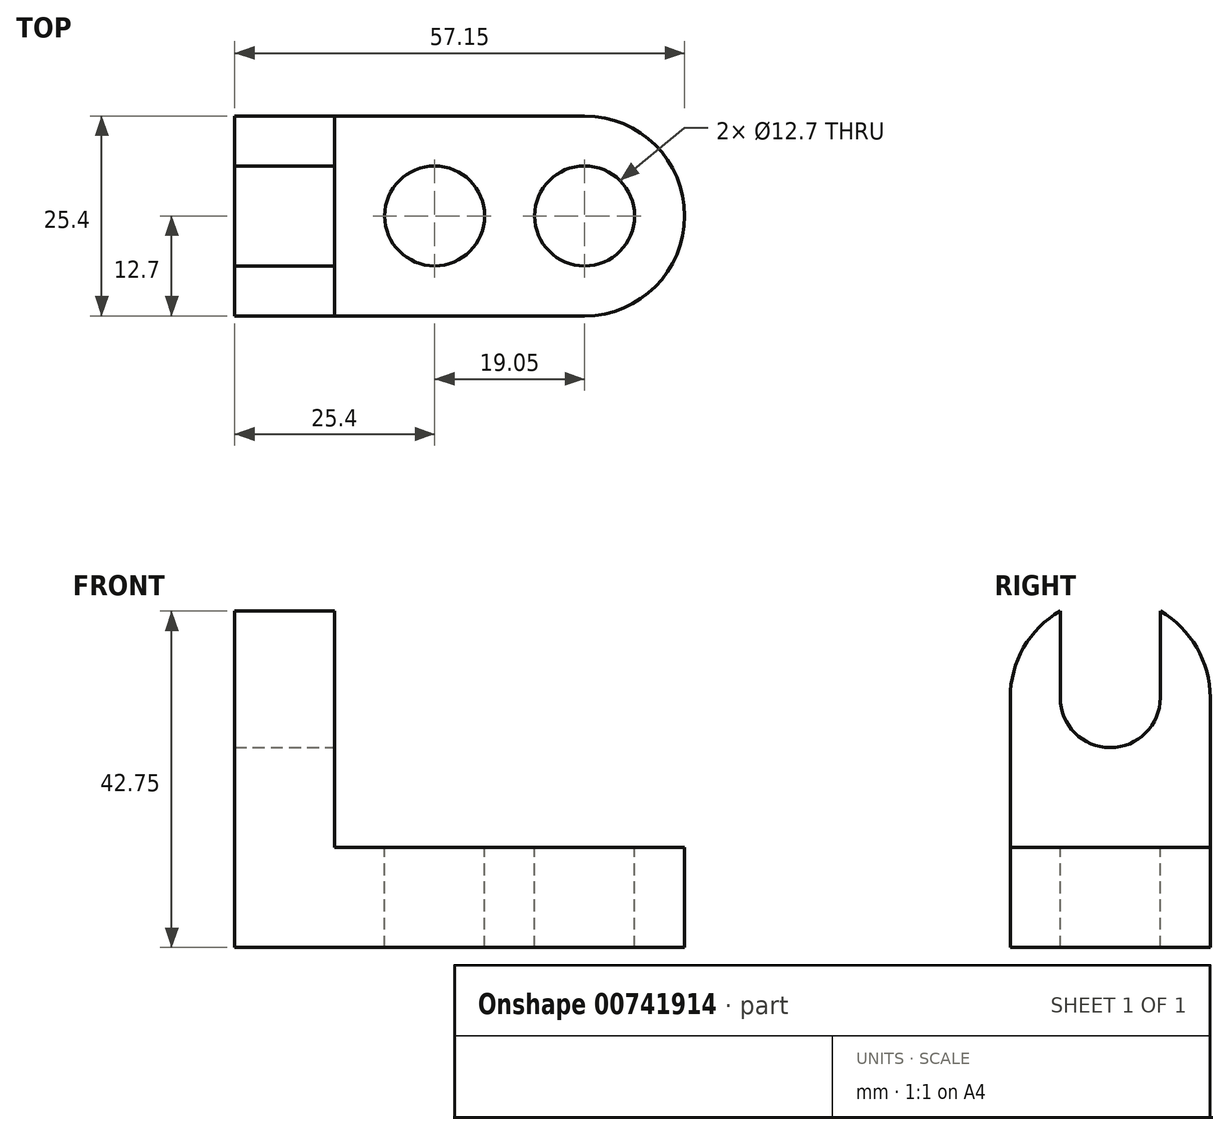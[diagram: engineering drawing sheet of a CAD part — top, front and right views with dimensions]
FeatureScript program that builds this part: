
annotation { "Feature Type Name" : "Feature", "Feature Type Description" : "" }
export const myFeature = defineFeature(function(context is Context, id is Id, definition is map)
    precondition{}
    {
        {
            var Q0;
            Q0=qCreatedBy(makeId("Front.planeOp"),FACE);
            var sketch = newSketch(context, id + "F0", { "sketchPlane" : qUnion([Q0])});
            skLineSegment(sketch, "E0", {"start": v(0, 44.45) * mm, "end": v(0, 0) * mm});
            skLineSegment(sketch, "E1", {"start": v(0, 0) * mm, "end": v(57.15, 0) * mm});
            skLineSegment(sketch, "E2", {"start": v(57.15, 0) * mm, "end": v(57.15, 12.7) * mm});
            skLineSegment(sketch, "E3", {"start": v(57.15, 12.7) * mm, "end": v(12.7, 12.7) * mm});
            skLineSegment(sketch, "E4", {"start": v(12.7, 12.7) * mm, "end": v(12.7, 44.45) * mm});
            skLineSegment(sketch, "E5", {"start": v(12.7, 44.45) * mm, "end": v(0, 44.45) * mm});
            skSolve(sketch);
        }
        {
            var Q0;
            Q0=makeQuery(id+"F0.imprint","IMPRINT",FACE,{"disambiguationData":[TD([[makeQuery(id+"F0.imprint","IMPRINT",EDGE,{"derivedFrom":sQuery(id+"F0.wireOp",EDGE,"E0")}),1.0]])]});
            extrude(context, id + "F1", {"entities" : qUnion([Q0]), "depth" : 25.4 * mm, "offsetDistance" : 25.4 * mm});
        }
        {
            var Q0;
            Q0=makeQuery(id+"F1.opExtrude","SWEPT_FACE",FACE,{"disambiguationData":[OSD([sQuery(id+"F0.wireOp",EDGE,"E4")])]});
            var sketch = newSketch(context, id + "F2", { "sketchPlane" : qUnion([Q0])});
            skLineSegment(sketch, "E6", {"start": v(-25.4, 31.75) * mm, "end": v(0, 31.75) * mm});
            skLineSegment(sketch, "E7", {"start": v(-25.4, 31.75) * mm, "end": v(-25.4, 44.45) * mm});
            skCircle(sketch, "E8", {"center": v(-12.7, 31.75) * mm, "radius": 6.35 * mm});
            skArc(sketch, "E9", {"start": v(0, 31.75) * mm, "mid": v(-12.7, 44.45) * mm, "end": v(-25.4, 31.75) * mm});
            skSolve(sketch);
        }
        {
            var Q0;
            {var subQ0=sQuery(id+"F2.wireOp",EDGE,"E8");var subQ1=sQuery(id+"F2.wireOp",EDGE,"E6");var subQ2=makeQuery(id+"F2.imprint","INTERSECT",VERTEX,{"disambiguationData":[OD(0.0)],"derivedFrom":[subQ1,subQ0]});Q0=makeQuery(id+"F2.imprint","IMPRINT",FACE,{"disambiguationData":[TD([[makeQuery(id+"F2.imprint","IMPRINT",EDGE,{"disambiguationData":[TD([[subQ2,-1.0]])],"derivedFrom":subQ1}),1.0]])]});}
            var Q1;
            {var subQ0=sQuery(id+"F2.wireOp",EDGE,"E8");var subQ1=sQuery(id+"F2.wireOp",EDGE,"E6");var subQ2=makeQuery(id+"F2.imprint","INTERSECT",VERTEX,{"disambiguationData":[OD(0.0)],"derivedFrom":[subQ1,subQ0]});Q1=makeQuery(id+"F2.imprint","IMPRINT",FACE,{"disambiguationData":[TD([[makeQuery(id+"F2.imprint","IMPRINT",EDGE,{"disambiguationData":[TD([[subQ2,-1.0]])],"derivedFrom":subQ1}),-1.0]])]});}
            var Q2;
            {var subQ0=sQuery(id+"F2.wireOp",EDGE,"E7");Q2=makeQuery(id+"F2.imprint","IMPRINT",FACE,{"disambiguationData":[TD([[makeQuery(id+"F2.imprint","IMPRINT",EDGE,{"derivedFrom":subQ0}),-1.0]])]});}
            var Q3;
            {var subQ0=sQuery(id+"F2.wireOp",EDGE,"E9");var subQ1=sQuery(id+"F0.wireOp",EDGE,"E4");var subQ2=makeQuery(id+"F1.opExtrude","CAP_EDGE",EDGE,{"disambiguationData":[OSD([subQ1])],"isStart":true});var subQ3=makeQuery(id+"F2.imprint","INTERSECT",VERTEX,{"derivedFrom":[subQ2,sQuery(id+"F2.wireOp",EDGE,"E6"),subQ0]});Q3=makeQuery(id+"F2.imprint","IMPRINT",FACE,{"disambiguationData":[TD([[makeQuery(id+"F2.imprint","IMPRINT",EDGE,{"disambiguationData":[TD([[subQ3,-1.0]])],"derivedFrom":subQ0}),-1.0]])]});}
            extrude(context, id + "F3", {"entities" : qUnion([Q0, Q1, Q2, Q3]), "operationType" : NewBodyOperationType.REMOVE, "endBound" : BoundingType.THROUGH_ALL, "oppositeDirection" : true, "depth" : 25.4 * mm, "offsetDistance" : 25.4 * mm});
        }
        {
            var Q0;
            Q0=makeQuery(id+"F1.opExtrude","SWEPT_FACE",FACE,{"disambiguationData":[OSD([sQuery(id+"F0.wireOp",EDGE,"E4")])]});
            var sketch = newSketch(context, id + "F4", { "sketchPlane" : qUnion([Q0])});
            skLineSegment(sketch, "E10", {"start": v(-19.05, 31.75) * mm, "end": v(-19.05, 42.75) * mm});
            skLineSegment(sketch, "E11", {"start": v(-6.35, 31.75) * mm, "end": v(-6.35, 42.75) * mm});
            skSolve(sketch);
        }
        {
            var Q0;
            {var subQ0=sQuery(id+"F4.wireOp",EDGE,"E10");Q0=makeQuery(id+"F4.imprint","IMPRINT",FACE,{"disambiguationData":[TD([[makeQuery(id+"F4.imprint","IMPRINT",EDGE,{"derivedFrom":subQ0}),-1.0]])]});}
            extrude(context, id + "F5", {"entities" : qUnion([Q0]), "operationType" : NewBodyOperationType.REMOVE, "endBound" : BoundingType.THROUGH_ALL, "oppositeDirection" : true, "depth" : 25.4 * mm, "offsetDistance" : 25.4 * mm});
        }
        {
            var Q0;
            Q0=makeQuery(id+"F1.opExtrude","SWEPT_FACE",FACE,{"disambiguationData":[OSD([sQuery(id+"F0.wireOp",EDGE,"E3")])]});
            var sketch = newSketch(context, id + "F6", { "sketchPlane" : qUnion([Q0])});
            skLineSegment(sketch, "E12", {"start": v(12.7, 0) * mm, "end": v(25.4, 0) * mm});
            skLineSegment(sketch, "E13", {"start": v(25.4, 0) * mm, "end": v(25.4, -25.4) * mm});
            skCircle(sketch, "E14", {"center": v(25.4, -12.7) * mm, "radius": 6.35 * mm});
            skLineSegment(sketch, "E15", {"start": v(57.15, 0) * mm, "end": v(44.45, 0) * mm});
            skLineSegment(sketch, "E16", {"start": v(44.45, 0) * mm, "end": v(44.45, -25.4) * mm});
            skCircle(sketch, "E17", {"center": v(44.45, -12.7) * mm, "radius": 6.35 * mm});
            skArc(sketch, "E18", {"start": v(44.45, -25.4) * mm, "mid": v(57.15, -12.7) * mm, "end": v(44.45, 0) * mm});
            skSolve(sketch);
        }
        {
            var Q0;
            {var subQ0=sQuery(id+"F6.wireOp",EDGE,"E14");var subQ1=sQuery(id+"F6.wireOp",EDGE,"E13");var subQ2=makeQuery(id+"F6.imprint","INTERSECT",VERTEX,{"disambiguationData":[OD(0.0)],"derivedFrom":[subQ1,subQ0]});Q0=makeQuery(id+"F6.imprint","IMPRINT",FACE,{"disambiguationData":[TD([[makeQuery(id+"F6.imprint","IMPRINT",EDGE,{"disambiguationData":[TD([[subQ2,-1.0]])],"derivedFrom":subQ1}),-1.0]])]});}
            var Q1;
            {var subQ0=sQuery(id+"F6.wireOp",EDGE,"E14");var subQ1=sQuery(id+"F6.wireOp",EDGE,"E13");var subQ2=makeQuery(id+"F6.imprint","INTERSECT",VERTEX,{"disambiguationData":[OD(0.0)],"derivedFrom":[subQ1,subQ0]});Q1=makeQuery(id+"F6.imprint","IMPRINT",FACE,{"disambiguationData":[TD([[makeQuery(id+"F6.imprint","IMPRINT",EDGE,{"disambiguationData":[TD([[subQ2,-1.0]])],"derivedFrom":subQ1}),1.0]])]});}
            var Q2;
            {var subQ0=sQuery(id+"F6.wireOp",EDGE,"E16");var subQ1=sQuery(id+"F6.wireOp",EDGE,"E17");var subQ2=makeQuery(id+"F6.imprint","INTERSECT",VERTEX,{"disambiguationData":[OD(0.0)],"derivedFrom":[subQ1,subQ0]});Q2=makeQuery(id+"F6.imprint","IMPRINT",FACE,{"disambiguationData":[TD([[makeQuery(id+"F6.imprint","IMPRINT",EDGE,{"disambiguationData":[TD([[subQ2,-1.0]])],"derivedFrom":subQ1}),1.0]])]});}
            var Q3;
            {var subQ0=sQuery(id+"F6.wireOp",EDGE,"E16");var subQ1=sQuery(id+"F6.wireOp",EDGE,"E17");var subQ2=makeQuery(id+"F6.imprint","INTERSECT",VERTEX,{"disambiguationData":[OD(0.0)],"derivedFrom":[subQ1,subQ0]});Q3=makeQuery(id+"F6.imprint","IMPRINT",FACE,{"disambiguationData":[TD([[makeQuery(id+"F6.imprint","IMPRINT",EDGE,{"disambiguationData":[TD([[subQ2,1.0]])],"derivedFrom":subQ1}),1.0]])]});}
            var Q4;
            {var subQ0=sQuery(id+"F6.wireOp",EDGE,"E15");Q4=makeQuery(id+"F6.imprint","IMPRINT",FACE,{"disambiguationData":[TD([[makeQuery(id+"F6.imprint","IMPRINT",EDGE,{"derivedFrom":subQ0}),1.0]])]});}
            var Q5;
            {var subQ0=sQuery(id+"F6.wireOp",EDGE,"E18");var subQ1=sQuery(id+"F0.wireOp",EDGE,"E3");var subQ2=makeQuery(id+"F1.opExtrude","CAP_EDGE",EDGE,{"disambiguationData":[OSD([subQ1])],"isStart":false});var subQ3=makeQuery(id+"F6.imprint","INTERSECT",VERTEX,{"derivedFrom":[subQ2,sQuery(id+"F6.wireOp",EDGE,"E16"),subQ0]});Q5=makeQuery(id+"F6.imprint","IMPRINT",FACE,{"disambiguationData":[TD([[makeQuery(id+"F6.imprint","IMPRINT",EDGE,{"disambiguationData":[TD([[subQ3,-1.0]])],"derivedFrom":subQ0}),-1.0]])]});}
            extrude(context, id + "F7", {"entities" : qUnion([Q0, Q1, Q2, Q3, Q4, Q5]), "operationType" : NewBodyOperationType.REMOVE, "endBound" : BoundingType.THROUGH_ALL, "oppositeDirection" : true, "depth" : 25.4 * mm, "offsetDistance" : 25.4 * mm});
        }
    });
